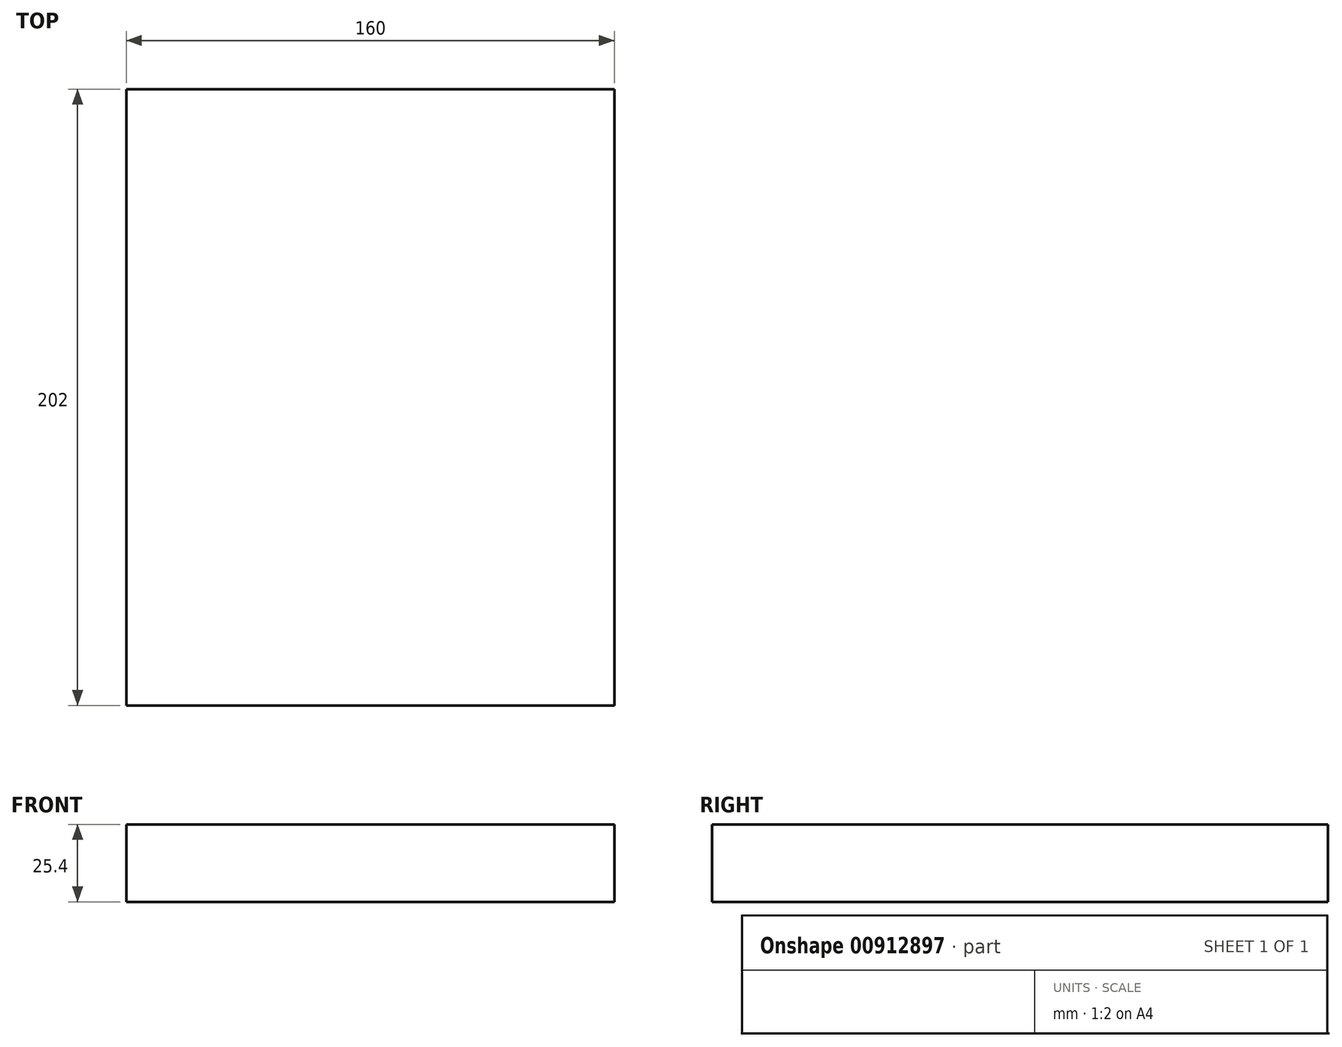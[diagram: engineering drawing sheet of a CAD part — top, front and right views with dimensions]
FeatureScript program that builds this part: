
annotation { "Feature Type Name" : "Feature", "Feature Type Description" : "" }
export const myFeature = defineFeature(function(context is Context, id is Id, definition is map)
    precondition{}
    {
        {
            var Q0;
            Q0=qCreatedBy(makeId("Top.planeOp"),FACE);
            var sketch = newSketch(context, id + "F0", { "sketchPlane" : qUnion([Q0])});
            skLineSegment(sketch, "E0.bottom", {"start": v(-231.03, 134.04) * mm, "end": v(-71.03, 134.04) * mm});
            skLineSegment(sketch, "E0.top", {"start": v(-231.03, -67.96) * mm, "end": v(-71.03, -67.96) * mm});
            skLineSegment(sketch, "E0.left", {"start": v(-231.03, 134.04) * mm, "end": v(-231.03, -67.96) * mm});
            skLineSegment(sketch, "E0.right", {"start": v(-71.03, 134.04) * mm, "end": v(-71.03, -67.96) * mm});
            skSolve(sketch);
        }
        {
            var Q0;
            Q0=makeQuery(id+"F0.imprint","IMPRINT",FACE,{"disambiguationData":[TD([[makeQuery(id+"F0.imprint","IMPRINT",EDGE,{"derivedFrom":sQuery(id+"F0.wireOp",EDGE,"E0.bottom")}),-1.0]])]});
            extrude(context, id + "F1", {"entities" : qUnion([Q0]), "depth" : 25.4 * mm, "offsetDistance" : 25 * mm});
        }
    });
